# Revit family: Two Door Units
name_source: partatom
category: Furniture
revit_build: Autodesk Revit 2018 (Build: 20181011_1500(x64)
units: mm (PartAtom-declared; Revit-internal decimal feet)

## family parameters
Always vertical = Yes
Cut with Voids When Loaded = No
OmniClass Number = 23.40.20.00
OmniClass Title = General Furniture and Specialties
Room Calculation Point = No
Shared = No
Work Plane-Based = No

## types (32) — shared parameters
Carcass_Material = Steel, Mild
Category = Furniture
Compliance Standards Certification = BS EN 14073 2004 Part 2 & 3, BS EN 14074, BS 4875 1998 Part 7 level 4 & Part 8, BS 476 Part 7 1987 Class 2Y
Door_Material = Steel, Mild
Expected Life = <10 Years
Finish = Powder Coated
Lock_Material = Steel AISI 4620
Manufacturer = Bisley
Range = LateralFile
Revision = V1
Routine Maintenance = We recommend you clean your unit with warm water and a mild detergent solution. A damp cloth can be used to remove dust particles.
URL = www.bisley.com
Uniclass 2015 Code = PR_40_30_78_57
Uniclass2015Title = Shelves and Storage Units
Uniclass2015Version = V1.1
Warranty = 10 Years
zero-valued in all types: Cost

## per-type parameters (varying)
| type | Carcass Type | Dimensions | Left Door Type | Right Door Right | Right Door Type | Weight |
| 08D20 | Carcasses : 08C20 | 800mm x 693mm x 470mm | Left Door 2 : 08D20 Right Door | 779 mm  [stored 2.55577 ft] | Right Door : 08D20 Right Door | 31.696 kg |
| 08D24 | Carcasses : 08C24 | 800mm x 845mm x 470mm | Left Door 2 : 08D24 Right Door | 779 mm  [stored 2.55577 ft] | Right Door : 08D24 Right Door | 36.33 kg |
| 08D30 | Carcasses : 08C30 | 800mm x 997mm x 470mm | Left Door 2 : 08D30 Right Door | 779 mm  [stored 2.55577 ft] | Right Door : 08D30 Right Door | 49.313 kg |
| 08D32 | Carcasses : 08C32 | 800mm x 1073mm x 470mm | Left Door 2 : 08D32 Right Door | 779 mm  [stored 2.55577 ft] | Right Door : 08D32 Right Door | 43.525 kg |
| 08D34 | Carcasses : 08C34 | 800mm x 1149mm x 470mm | Left Door 2 : 08D34 Left Door | 779 mm  [stored 2.55577 ft] | Right Door : 08D34 Right Door | 47.3 kg |
| 08D36 | Carcasses : 08C36 | 800mm x 1125mm x 470mm | Left Door 2 : 08D36 Right Door | 779 mm  [stored 2.55577 ft] | Right Door : 08D36 Right Door | 48.606 kg |
| 08D40 | Carcasses : 08C40 | 800mm x 1301mm x 470mm | Left Door 2 : 08D40 Right Door | 779 mm  [stored 2.55577 ft] | Right Door : 08D40 Right Door | 49.342 kg |
| 08D43 | Carcasses : 08C43 | 800mm x 1415mm x 470mm | Left Door 2 : 08D43 Right Door | 779 mm  [stored 2.55577 ft] | Right Door : 08D43 Right Door | 53.184 kg |
| 08D50 | Carcasses : 08C50 | 800mm x 1643mm x 470mm | Left Door 2 : 08D50 Left Door | 779 mm  [stored 2.55577 ft] | Right Door : 08D50 Right Door | 59.438 kg |
| 08D54 | Carcasses : 08C54 | 800mm x 1795mm x 470mm | Left Door 2 : 08D54 Left Door | 779 mm  [stored 2.55577 ft] | Right Door : 08D54 Right Door | 65.208 kg |
| 09D60 | Carcasses : 09C60 | 900mm x 1947mm x 470mm | Left Door 2 : 09D60 Left Door | 879 mm  [stored 2.88386 ft] | Right Door : 09D60 Right Door | 72.985 kg |
| 08D64 | Carcasses : 08C64 | 800mm x 2099mm x 470mm | Left Door 2 : 08D64 Left Door | 779 mm  [stored 2.55577 ft] | Right Door : 08D64 Right Door | 72.023 kg |
| 08DD21 | Carcasses : 08DD21 | 800mm x 718mm x 470mm | Left Door 2 : 08DD21 Left Door | 779 mm  [stored 2.55577 ft] | Right Door : 08DD21 Right Door | 33.00 kg |
| 09D20 | Carcasses : 09C20 | 900mm x 693mm x 470mm | Left Door 2 : 09D20 Left Door | 879 mm  [stored 2.88386 ft] | Right Door : 09D20 Right Door | 34.816 kg |
| 09D30 | Carcasses : 09C30 | 900mm x 997mm x 470mm | Left Door 2 : 09D30 Left Door | 879 mm  [stored 2.88386 ft] | Right Door : 09D30 Right Door | 44.089 kg |
| 09D32 | Carcasses : 09C32 | 900mm x 1073mm x 470mm | Left Door 2 : 09D32 Left Door | 879 mm  [stored 2.88386 ft] | Right Door : 09D32 Right Door | 46.658 kg |
| 09D34 | Carcasses : 09C34 | 900mm x 1149mm x 470mm | Left Door 2 : 09D34 Left Door | 879 mm  [stored 2.88386 ft] | Right Door : 09D34 Right Door | 46.977 kg |
| 09D36 | Carcasses : 09C36 | 900mm x 1225mm x 470mm | Left Door 2 : 09D36 Left Door | 879 mm  [stored 2.88386 ft] | Right Door : 09D36 Right Door | 50.00 kg |
| 08D60 | Carcasses : 08C60 | 800mm x 1947mm x 470mm | Left Door 2 : 08D60 Left Door | 779 mm  [stored 2.55577 ft] | Right Door : 08D60 Right Door | 68.85 kg |
| 09D64 | Carcasses : 09C64 | 900mm x 2099mm x 470mm | Left Door 2 : 09D64 Left Door | 879 mm  [stored 2.88386 ft] | Right Door : 10D64 Right Door | 81.131 kg |
| 10D20 | Carcasses : 10C20 | 1000mm x 693mm x 470mm | Left Door 2 : 10D20 Left Door | 979 mm  [stored 3.21194 ft] | Right Door : 10D20 Right Door | 31.696 kg |
| 10D24 | Carcasses : 10C24 | 1000mm x 845mm x 470mm | Left Door 2 : 10D24 Left Door | 979 mm  [stored 3.21194 ft] | Right Door : 10D24 Right Door | 41.295 kg |
| 10D30 | Carcasses : 10C30 | 1000mm x 997mm x 470mm | Left Door 2 : 10D30 Left Door | 979 mm  [stored 3.21194 ft] | Right Door : 10D30 Right Door | 46.761 kg |
| 10D32 | Carcasses : 10C32 | 1000mm x 1073mm x 470mm | Left Door 2 : 10D32 Left Door | 979 mm  [stored 3.21194 ft] | Right Door : 10D32 Right Door | 49.89 kg |
| 10D34 | Carcasses : 10C34 | 1000mm x 1149mm x 470mm | Left Door 2 : 10D34 Left Door | 979 mm  [stored 3.21194 ft] | Right Door : 10D34 Right Door | 48.73 kg |
| 10D36 | Carcasses : 10C36 | 1000mm x 1125mm x 470mm | Left Door 2 : 10D36 Left Door | 979 mm  [stored 3.21194 ft] | Right Door : 10D36 Right Door | 56.644 kg |
| 10D40 | Carcasses : 10C40 | 1000mm x 1301mm x 470mm | Left Door 2 : 10D40 Left Door | 979 mm  [stored 3.21194 ft] | Right Door : 10D40 Right Door | 56.08 kg |
| 10D43 | Carcasses : 10C43 | 1000mm x 1415mm x 470mm | Left Door 2 : 10D43 Left Door | 979 mm  [stored 3.21194 ft] | Right Door : 10D43 Right Door | 53.184 kg |
| 10D64 | Carcasses : 10C64 | 1000mm x 2099mm x 470mm | Left Door 2 : 10D64 Left Door | 979 mm  [stored 3.21194 ft] | Right Door : 10D64 Right Door | 87.1 kg |
| 10D60 | Carcasses : 10C60 | 1000mm x 1947mm x 470mm | Left Door 2 : 10D60 Left Door | 979 mm  [stored 3.21194 ft] | Right Door : 10D60 Right Door | 77.553 kg |
| 10D54 | Carcasses : 10C54 | 1000mm x 1795mm x 470mm | Left Door 2 : 10D54 Left Door | 979 mm  [stored 3.21194 ft] | Right Door : 10D54 Right Door | 73.374 kg |
| 10D50 | Carcasses : 10C50 | 1000mm x 1643mm x 470mm | Left Door 2 : 10D50 Left Door | 979 mm  [stored 3.21194 ft] | Right Door : 10D50 Right Door | 67.433 kg |

note: column(s) folded — value = type name in every type: Model

note: [stored X ft] marks values corroborated as IEEE doubles in the binary element streams (Revit-internal decimal feet)

## geometry (parser evidence)
native form markers: Sweep x47
no freeform markers — native parametric forms only
